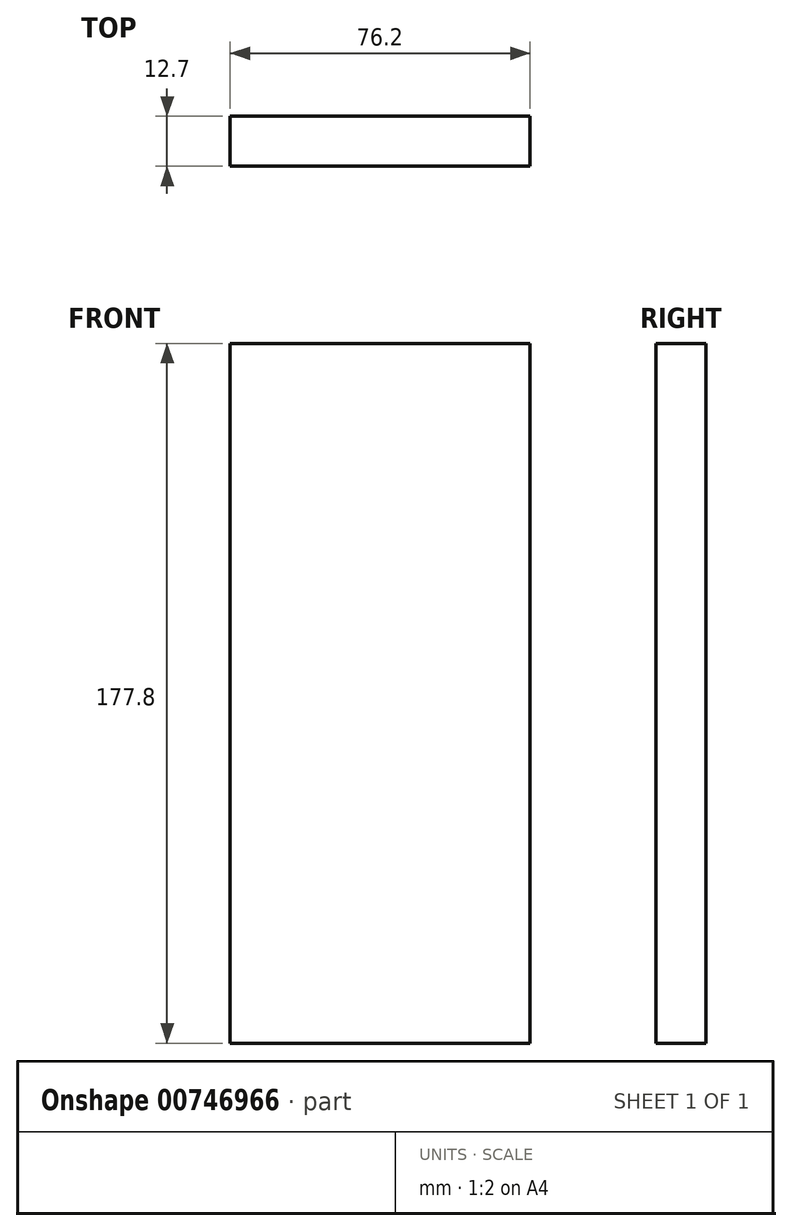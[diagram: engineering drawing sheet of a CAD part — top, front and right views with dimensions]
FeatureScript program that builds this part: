
annotation { "Feature Type Name" : "Feature", "Feature Type Description" : "" }
export const myFeature = defineFeature(function(context is Context, id is Id, definition is map)
    precondition{}
    {
        {
            var Q0;
            Q0=qCreatedBy(makeId("Front.planeOp"),FACE);
            var sketch = newSketch(context, id + "F0", { "sketchPlane" : qUnion([Q0])});
            skLineSegment(sketch, "E0.bottom", {"start": v(33.1, -52.87) * mm, "end": v(-43.1, -52.87) * mm});
            skLineSegment(sketch, "E0.top", {"start": v(33.1, 124.93) * mm, "end": v(-43.1, 124.93) * mm});
            skLineSegment(sketch, "E0.left", {"start": v(33.1, -52.87) * mm, "end": v(33.1, 124.93) * mm});
            skLineSegment(sketch, "E0.right", {"start": v(-43.1, -52.87) * mm, "end": v(-43.1, 124.93) * mm});
            skPoint(sketch, "E0.middle", {"position": v(-5, 36.03) * mm});
            skSolve(sketch);
        }
        {
            var Q0;
            Q0=makeQuery(id+"F0.imprint","IMPRINT",FACE,{"disambiguationData":[TD([[makeQuery(id+"F0.imprint","IMPRINT",EDGE,{"derivedFrom":sQuery(id+"F0.wireOp",EDGE,"E0.bottom")}),-1.0]])]});
            extrude(context, id + "F1", {"entities" : qUnion([Q0]), "depth" : 12.7 * mm, "offsetDistance" : 25.4 * mm});
        }
    });
